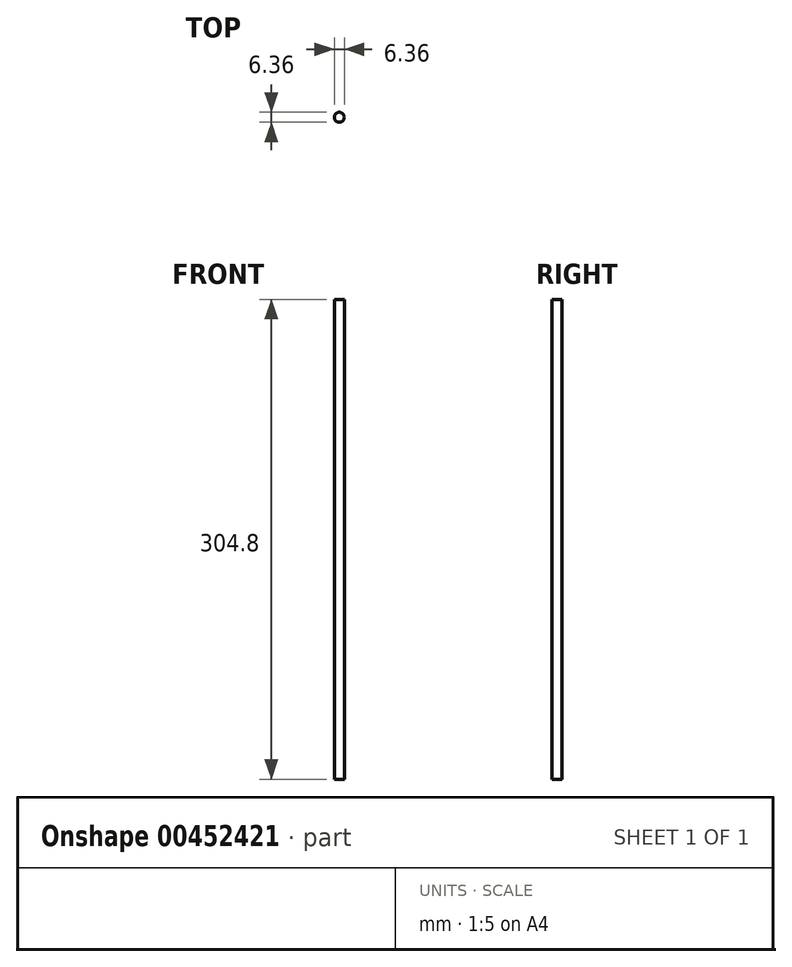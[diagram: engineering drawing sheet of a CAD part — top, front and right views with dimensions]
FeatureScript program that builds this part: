
annotation { "Feature Type Name" : "Feature", "Feature Type Description" : "" }
export const myFeature = defineFeature(function(context is Context, id is Id, definition is map)
    precondition{}
    {
        {
            var Q0;
            Q0=qCreatedBy(makeId("Top.planeOp"),FACE);
            var sketch = newSketch(context, id + "F0", { "sketchPlane" : qUnion([Q0])});
            skCircle(sketch, "E0", {"center": v(0, 0) * mm, "radius": 3.18 * mm});
            skSolve(sketch);
        }
        {
            var Q0;
            Q0=makeQuery(id+"F0.imprint","IMPRINT",FACE,{"disambiguationData":[TD([[makeQuery(id+"F0.imprint","IMPRINT",EDGE,{"derivedFrom":sQuery(id+"F0.wireOp",EDGE,"E0")}),1.0]])]});
            extrude(context, id + "F1", {"entities" : qUnion([Q0]), "depth" : 304.8 * mm});
        }
    });
